# Revit family: Siemens_MV_switchgear_gas-insulated_8DJH_compact  ring main and transformer panel
name_source: partatom
category: Electrical Fixtures
revit_build: Autodesk Revit 2016 (Build: 20150714_1515(x64)
units: mm (PartAtom-declared; Revit-internal decimal feet)

## family parameters
Always vertical = Yes
Cut with Voids When Loaded = No
Maintain Annotation Orientation = No
OmniClass Number = 23.80.00.00
OmniClass Title = Electric Power and Lighting
Part Type = Normal
Room Calculation Point = No
Round Connector Dimension = Use Diameter
Shared = No
Work Plane-Based = No

## types (3) — shared parameters
Capacitive voltage  indicator = with
Capacitive voltage indicator = CAPDIS-S1+;CAPDIS-S2+;HR;LRM;VOIS+;VOIS R+;WEGA 1.2 C;WEGA 2.2 C
Consultant support for Totally Integrated Power (TIP) = www.siemens.com/tip-cs
Edition number = 1
IFC Classification = Electric Distribution
Internal arc classification = IAC A F 21kA/1s; IAC A FLR 21kA/1s
Manufacturer = Siemens AG
Panel connection = One cable per phase
Product Guid = 4bded476-668d-478a-98aa-a03dbc06cb6d
Product data url = http://bimobject.com
Rated current feeder (A) = 630
Rated frequency (Hz) = 50;60
Rated lightning impulse withstand voltage (kV) = 60;75;95;125
Rated normal current busbar (A) = 630
Rated short-duration power-frequency withstand voltage (kV) = 20;28;36;38;50
Rated short-time withstand current (kA/s) = 16/1;16/3;20/1;20/3;25/1
Rated voltage (kV) = 3.3 - 22
SIMARIS planning tools = www.siemens.com/simaris
Short circuit/earth fault indicator = without; with
Specification texts = www.siemens.com/specifications
Standards = IEC / GOST / GB
Switchgear type = 8DJH compact
Technical description MV-switchgear = www.siemens.com/medium-voltage-switchgear
Three-position switch = manual operated; motor operated
Type of arrangement = wall-standing; free-standing
Voltage rating (kV) = 25 - 34.5

## per-type parameters (varying)
| type | Panel type | V | V3 | V4 |
| 4 ring main and 2 transformer panel (RRT-RRT) | RRT-RRT | 4 | No | Yes |
| 2 ring main and 1 transformer panel (RRT) | RRT | 2 | No | No |
| 3 ring main and 1 transformer panel (RRT-R) | RRT-R | 3 | Yes | No |

note: column(s) folded — value = type name in every type: Model

## geometry (parser evidence)
native form markers: Blend x9, Sweep x16
no freeform markers — native parametric forms only
